# Revit family: Столбик ограждения «Астана»
name_source: partatom
category: Антураж
revit_build: Autodesk Revit 2017 (Build: 20170118_1100(x64)
units: mm (PartAtom-declared; Revit-internal decimal feet)

## family parameters
Всегда вертикально = Да
Источник визуального образа = Геометрия семейства
На основе рабочей плоскости = Нет
Общий = Нет
При загрузке вырезать с полостями = Нет
Точка расчета площади = Нет

## types (3) — shared parameters
ADSK_Код изделия = 11375
ADSK_Материал = FS_Древесина_Лиственница тонированная_Груша
ADSK_Материал фурнитуры = FS_Металл_Оцинкованный_Хром
ADSK_Наименование = Столбик ограждения «Астана»
ADSK_Размер_Высота = 950 мм
ADSK_Размер_Ширина = 280 мм
URL = https://hobbyka.ru
Изготовитель = ООО "Хоббика"
zero-valued in all types: Высота

## per-type parameters (varying)
| type | Крючок_1 | Крючок_2 |
| Столбик ограждения «Астана»_Исполнение1 | Нет | Нет |
| Столбик ограждения «Астана»_Исполнение 2 | Да | Нет |
| Столбик ограждения «Астана»_Исполнение 3 | Да | Да |
